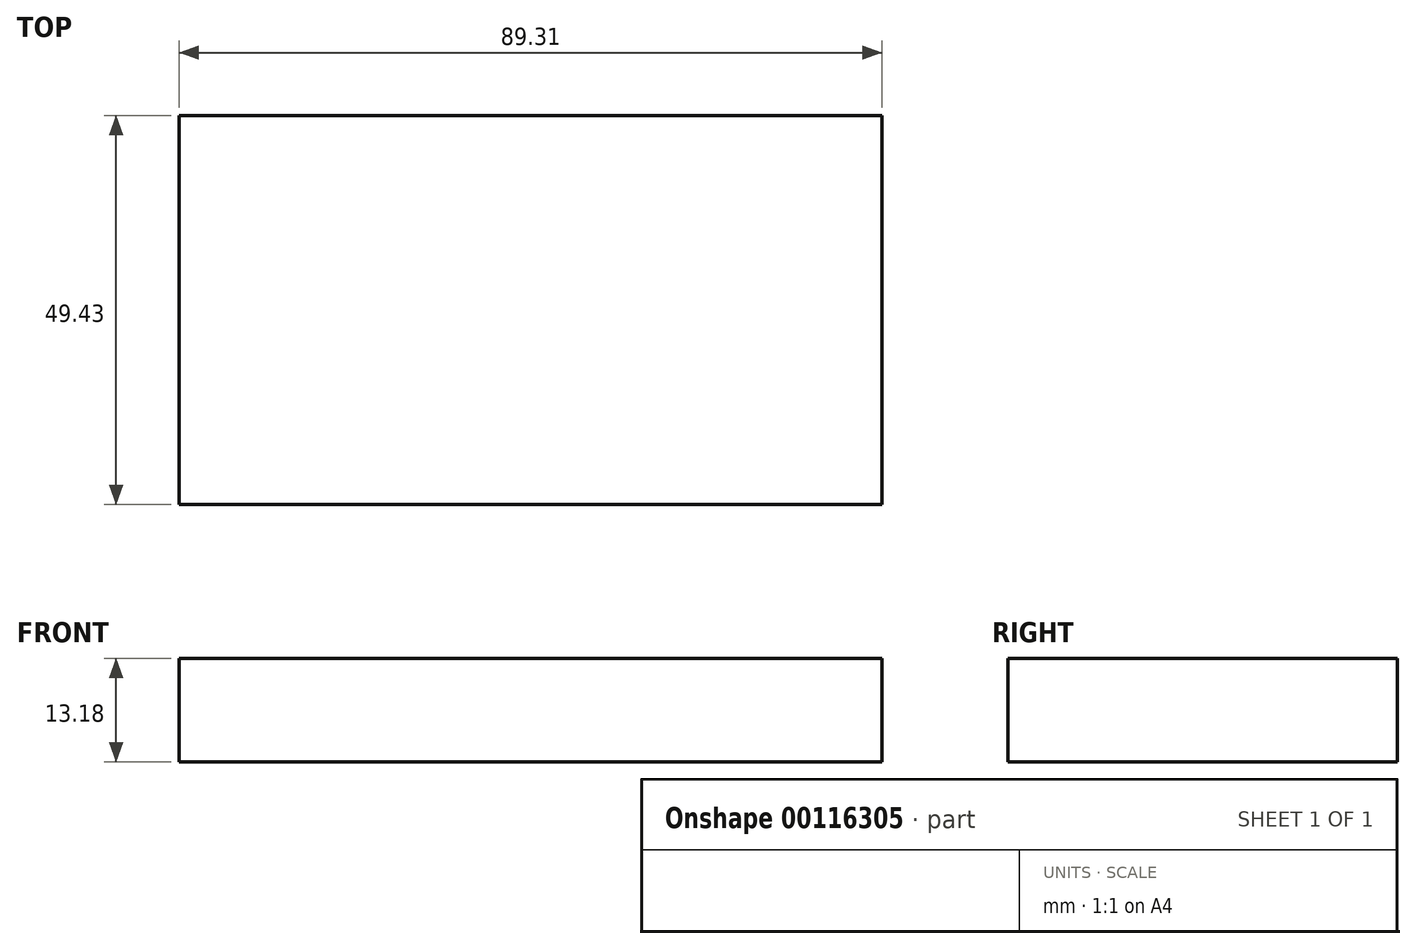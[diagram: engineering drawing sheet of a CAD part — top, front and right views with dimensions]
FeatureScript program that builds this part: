
annotation { "Feature Type Name" : "Feature", "Feature Type Description" : "" }
export const myFeature = defineFeature(function(context is Context, id is Id, definition is map)
    precondition{}
    {
        {
            var Q0;
            Q0=qCreatedBy(makeId("Top.planeOp"),FACE);
            var sketch = newSketch(context, id + "F0", { "sketchPlane" : qUnion([Q0])});
            skLineSegment(sketch, "E0.bottom", {"start": v(-35.9, 30.59) * mm, "end": v(53.41, 30.59) * mm});
            skLineSegment(sketch, "E0.top", {"start": v(-35.9, -18.84) * mm, "end": v(53.41, -18.84) * mm});
            skLineSegment(sketch, "E0.left", {"start": v(-35.9, 30.59) * mm, "end": v(-35.9, -18.84) * mm});
            skLineSegment(sketch, "E0.right", {"start": v(53.41, 30.59) * mm, "end": v(53.41, -18.84) * mm});
            skSolve(sketch);
        }
        {
            var Q0;
            Q0 = qSketchRegion(id + "F0", true);
            extrude(context, id + "F1", {"entities" : qUnion([Q0]), "depth" : 13.18 * mm});
        }
    });
